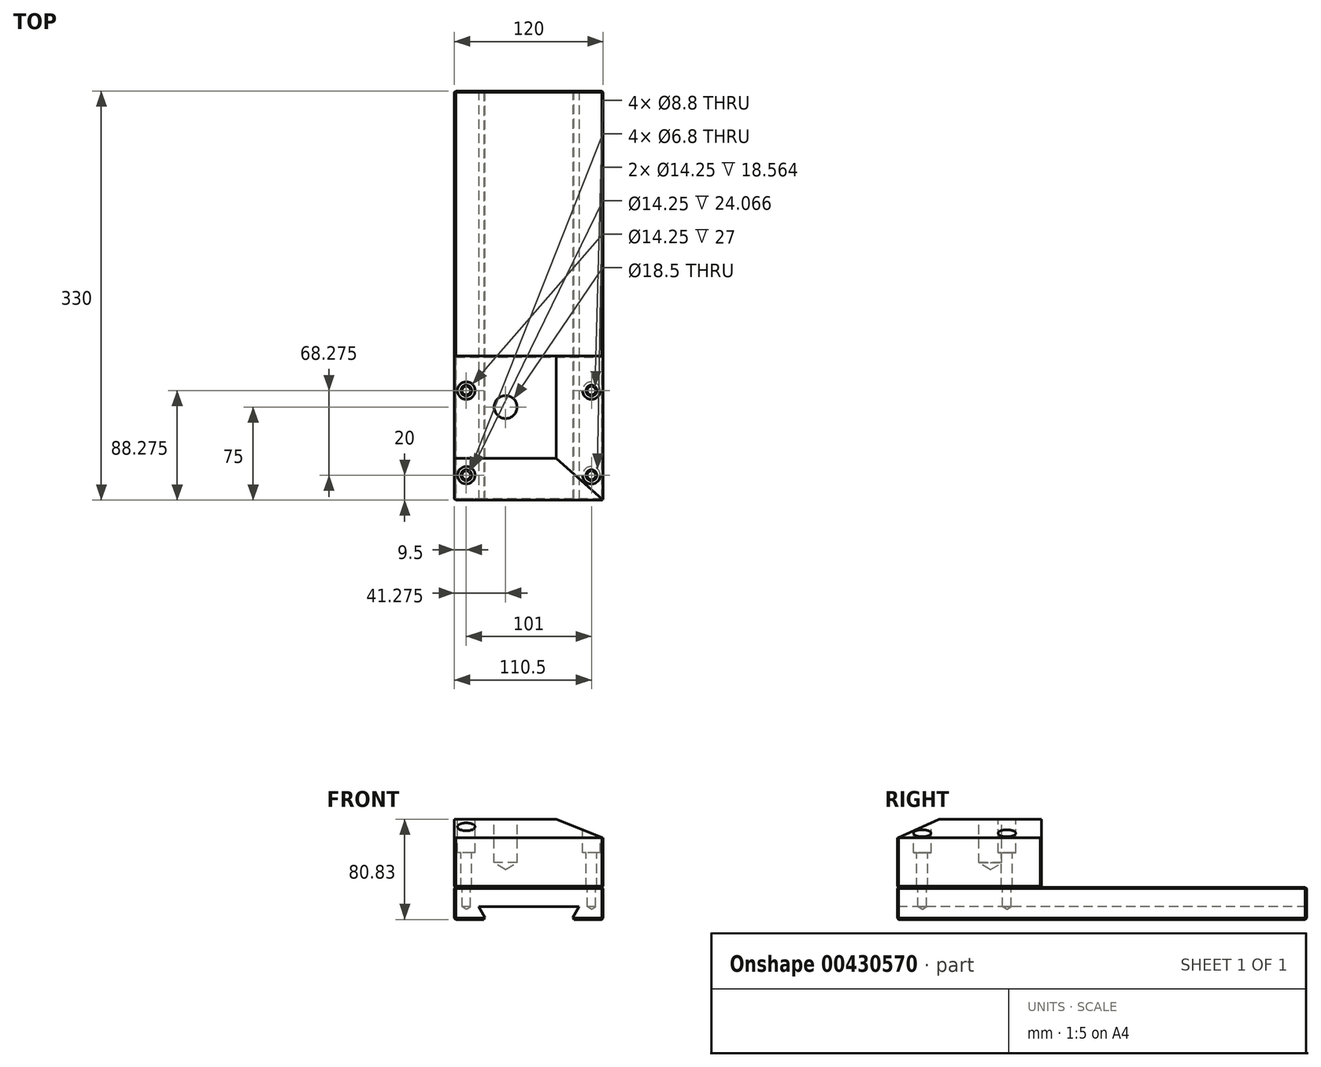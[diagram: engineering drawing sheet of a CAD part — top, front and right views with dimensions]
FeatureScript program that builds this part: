
annotation { "Feature Type Name" : "Feature", "Feature Type Description" : "" }
export const myFeature = defineFeature(function(context is Context, id is Id, definition is map)
    precondition{}
    {
        {
            var Q0;
            Q0=qCreatedBy(makeId("Front.planeOp"),FACE);
            var sketch = newSketch(context, id + "F0", { "sketchPlane" : qUnion([Q0])});
            skLineSegment(sketch, "E0.bottom", {"start": v(0, 0) * mm, "end": v(25.49, 0) * mm});
            skLineSegment(sketch, "E0.top", {"start": v(0, 26) * mm, "end": v(120, 26) * mm});
            skLineSegment(sketch, "E0.left", {"start": v(0, 0) * mm, "end": v(0, 26) * mm});
            skLineSegment(sketch, "E0.right", {"start": v(120, 0) * mm, "end": v(120, 26) * mm});
            skLineSegment(sketch, "E1", {"start": v(19.56, 10.27) * mm, "end": v(25.49, 0) * mm});
            skLineSegment(sketch, "E2", {"start": v(19.56, 10.27) * mm, "end": v(60, 10.27) * mm});
            skLineSegment(sketch, "E3", {"start": v(60, 10.27) * mm, "end": v(100.44, 10.27) * mm});
            skLineSegment(sketch, "E4", {"start": v(100.44, 10.27) * mm, "end": v(94.51, 0) * mm});
            skLineSegment(sketch, "E5", {"start": v(60, -6.52) * mm, "end": v(60, 31.96) * mm, "construction": true});
            skPoint(sketch, "E5.startSnap0", {"position": v(60, 0) * mm});
            skPoint(sketch, "E5.endSnap0", {"position": v(60, 26) * mm});
            skLineSegment(sketch, "E6.trimOffspring", {"start": v(94.51, 0) * mm, "end": v(120, 0) * mm});
            skSolve(sketch);
        }
        {
            var Q0;
            Q0=qSketchRegion(id+"F0",true);
            var Q1;
            Q1=makeQuery(id+"F0.imprint","IMPRINT",FACE,{"disambiguationData":[TD([[makeQuery(id+"F0.imprint","IMPRINT",EDGE,{"derivedFrom":sQuery(id+"F0.wireOp",EDGE,"E0.bottom")}),1.0]])]});
            extrude(context, id + "F1", {"entities" : qUnion([Q0, Q1]), "oppositeDirection" : true, "depth" : 330 * mm});
        }
        {
            var Q0;
            Q0=makeQuery(id+"F1.opExtrude","CAP_FACE",FACE,{"disambiguationData":[OSD([sQuery(id+"F0.wireOp",EDGE,"E0.bottom"),sQuery(id+"F0.wireOp",EDGE,"E0.top"),sQuery(id+"F0.wireOp",EDGE,"E0.left"),sQuery(id+"F0.wireOp",EDGE,"E0.right"),sQuery(id+"F0.wireOp",EDGE,"E1"),sQuery(id+"F0.wireOp",EDGE,"E2"),sQuery(id+"F0.wireOp",EDGE,"E3"),sQuery(id+"F0.wireOp",EDGE,"E4"),sQuery(id+"F0.wireOp",EDGE,"E6.trimOffspring")])],"isStart":true});
            var sketch = newSketch(context, id + "F2", { "sketchPlane" : qUnion([Q0])});
            skLineSegment(sketch, "E7.bottom", {"start": v(0, 26) * mm, "end": v(120, 26) * mm});
            skLineSegment(sketch, "E7.top", {"start": v(0, 80.83) * mm, "end": v(120, 80.83) * mm});
            skLineSegment(sketch, "E7.left", {"start": v(0, 26) * mm, "end": v(0, 80.83) * mm});
            skLineSegment(sketch, "E7.right", {"start": v(120, 26) * mm, "end": v(120, 80.83) * mm});
            skSolve(sketch);
        }
        {
            var Q0;
            Q0=makeQuery(id+"F1.opExtrude","SWEPT_EDGE",EDGE,{"disambiguationData":[OSD([sQuery(id+"F0.wireOp",EDGE,"E0.top"),sQuery(id+"F0.wireOp",EDGE,"E0.left")])]});
            var Q1;
            Q1=makeQuery(id+"F1.opExtrude","SWEPT_EDGE",EDGE,{"disambiguationData":[OSD([sQuery(id+"F0.wireOp",EDGE,"E0.top"),sQuery(id+"F0.wireOp",EDGE,"E0.right")])]});
            var Q2;
            Q2=makeQuery(id+"F1.opExtrude","CAP_EDGE",EDGE,{"disambiguationData":[OSD([sQuery(id+"F0.wireOp",EDGE,"E0.left")])],"isStart":true});
            var Q3;
            Q3=makeQuery(id+"F1.opExtrude","CAP_EDGE",EDGE,{"disambiguationData":[OSD([sQuery(id+"F0.wireOp",EDGE,"E0.right")])],"isStart":true});
            var Q4;
            Q4=makeQuery(id+"F1.opExtrude","CAP_EDGE",EDGE,{"disambiguationData":[OSD([sQuery(id+"F0.wireOp",EDGE,"E6.trimOffspring")])],"isStart":true});
            var Q5;
            Q5=makeQuery(id+"F1.opExtrude","CAP_EDGE",EDGE,{"disambiguationData":[OSD([sQuery(id+"F0.wireOp",EDGE,"E0.bottom")])],"isStart":true});
            var Q6;
            Q6=makeQuery(id+"F1.opExtrude","SWEPT_EDGE",EDGE,{"disambiguationData":[OSD([sQuery(id+"F0.wireOp",EDGE,"E0.bottom"),sQuery(id+"F0.wireOp",EDGE,"E0.left")])]});
            var Q7;
            Q7=makeQuery(id+"F1.opExtrude","CAP_EDGE",EDGE,{"disambiguationData":[OSD([sQuery(id+"F0.wireOp",EDGE,"E0.bottom")])],"isStart":false});
            var Q8;
            Q8=makeQuery(id+"F1.opExtrude","CAP_EDGE",EDGE,{"disambiguationData":[OSD([sQuery(id+"F0.wireOp",EDGE,"E0.left")])],"isStart":false});
            var Q9;
            Q9=makeQuery(id+"F1.opExtrude","CAP_EDGE",EDGE,{"disambiguationData":[OSD([sQuery(id+"F0.wireOp",EDGE,"E0.top")])],"isStart":false});
            var Q10;
            Q10=makeQuery(id+"F1.opExtrude","CAP_EDGE",EDGE,{"disambiguationData":[OSD([sQuery(id+"F0.wireOp",EDGE,"E6.trimOffspring")])],"isStart":false});
            var Q11;
            Q11=makeQuery(id+"F1.opExtrude","CAP_EDGE",EDGE,{"disambiguationData":[OSD([sQuery(id+"F0.wireOp",EDGE,"E0.right")])],"isStart":false});
            var Q12;
            Q12=makeQuery(id+"F1.opExtrude","SWEPT_EDGE",EDGE,{"disambiguationData":[OSD([sQuery(id+"F0.wireOp",EDGE,"E0.right"),sQuery(id+"F0.wireOp",EDGE,"E6.trimOffspring")])]});
            var Q13;
            Q13=makeQuery(id+"F1.opExtrude","SWEPT_EDGE",EDGE,{"disambiguationData":[OSD([sQuery(id+"F0.wireOp",EDGE,"E4"),sQuery(id+"F0.wireOp",EDGE,"E6.trimOffspring")])]});
            var Q14;
            Q14=makeQuery(id+"F1.opExtrude","SWEPT_EDGE",EDGE,{"disambiguationData":[OSD([sQuery(id+"F0.wireOp",EDGE,"E0.bottom"),sQuery(id+"F0.wireOp",EDGE,"E1")])]});
            var Q15;
            Q15=makeQuery(id+"F1.opExtrude","CAP_EDGE",EDGE,{"disambiguationData":[OSD([sQuery(id+"F0.wireOp",EDGE,"E0.top")])],"isStart":true});
            chamfer(context, id + "F3", {"entities" : qUnion([Q0, Q1, Q2, Q3, Q4, Q5, Q6, Q7, Q8, Q9, Q10, Q11, Q12, Q13, Q14, Q15]), "width" : 1 * mm, "tangentPropagation" : true});
        }
        {
            var Q0;
            Q0=qSketchRegion(id+"F2",true);
            extrude(context, id + "F4", {"entities" : qUnion([Q0]), "oppositeDirection" : true, "depth" : 116.28 * mm});
        }
        {
            var Q0;
            Q0=makeQuery(id+"F4.opExtrude","SWEPT_FACE",FACE,{"disambiguationData":[OSD([sQuery(id+"F2.wireOp",EDGE,"E7.top")])]});
            var sketch = newSketch(context, id + "F5", { "sketchPlane" : qUnion([Q0])});
            skLineSegment(sketch, "E8.bottom", {"start": v(9.5, 88.27) * mm, "end": v(110.5, 88.28) * mm, "construction": true});
            skLineSegment(sketch, "E8.top", {"start": v(9.5, 20) * mm, "end": v(110.5, 20) * mm, "construction": true});
            skLineSegment(sketch, "E8.left", {"start": v(9.5, 88.27) * mm, "end": v(9.5, 20) * mm, "construction": true});
            skLineSegment(sketch, "E8.right", {"start": v(110.5, 88.28) * mm, "end": v(110.5, 20) * mm, "construction": true});
            skPoint(sketch, "E9", {"position": v(9.5, 88.27) * mm});
            skPoint(sketch, "E10", {"position": v(110.5, 88.28) * mm});
            skPoint(sketch, "E11", {"position": v(110.5, 20) * mm});
            skPoint(sketch, "E12", {"position": v(9.5, 20) * mm});
            skPoint(sketch, "E13", {"position": v(41.27, 75) * mm});
            skPoint(sketch, "E13.positionSnap0", {"position": v(60, 88.28) * mm});
            skPoint(sketch, "E13.positionSnap1", {"position": v(120, 58.14) * mm});
            skSolve(sketch);
        }
        {
            var Q0;
            Q0=sQuery(id+"F5.wireOp",VERTEX,"E8.bottom.start");
            var Q1;
            Q1=sQuery(id+"F5.wireOp",VERTEX,"E12");
            var Q2;
            Q2=makeQuery(id+"F4.opExtrude","SWEPT_BODY",BODY,{"disambiguationData":[OSD([sQuery(id+"F2.wireOp",EDGE,"E7.bottom"),sQuery(id+"F2.wireOp",EDGE,"E7.top"),sQuery(id+"F2.wireOp",EDGE,"E7.left"),sQuery(id+"F2.wireOp",EDGE,"E7.right")])]});
            hole(context, id + "F6", {"style" : HoleStyle.C_BORE, "endStyle" : HoleEndStyle.THROUGH, "holeDiameter" : 8.8 * mm, "cBoreDiameter" : 14.25 * mm, "cBoreDepth" : 27 * mm, "isTappedThrough" : true, "tappedDepth" : 12 * mm, "tapClearance" : 3, "startFromSketch" : true, "locations" : qUnion([Q0, Q1]), "scope" : qUnion([Q2])});
        }
        {
            var Q0;
            Q0=sQuery(id+"F5.wireOp",VERTEX,"E13");
            var Q1;
            Q1=makeQuery(id+"F4.opExtrude","SWEPT_BODY",BODY,{"disambiguationData":[OSD([sQuery(id+"F2.wireOp",EDGE,"E7.bottom"),sQuery(id+"F2.wireOp",EDGE,"E7.top"),sQuery(id+"F2.wireOp",EDGE,"E7.left"),sQuery(id+"F2.wireOp",EDGE,"E7.right")])]});
            hole(context, id + "F7", {"style" : HoleStyle.SIMPLE, "endStyle" : HoleEndStyle.BLIND, "standardTappedOrClearance" : lookupTablePath({ "standard" : "ISO", "engagement" : "75%", "pitch" : "1.5 mm", "size" : "M20", "type" : "Tapped" }), "standardBlindInLast" : lookupTablePath({ "standard" : "ISO", "engagement" : "75%", "pitch" : "1.5 mm", "size" : "M20", "type" : "Tapped" }), "holeDiameter" : 18.5 * mm, "showTappedDepth" : true, "holeDepth" : 35 * mm, "isTappedThrough" : true, "tappedDepth" : 30.5 * mm, "tapClearance" : 3, "startFromSketch" : true, "locations" : qUnion([Q0]), "scope" : qUnion([Q1]), "majorDiameter" : 20 * mm});
        }
        {
            var Q0;
            Q0=makeQuery(id+"F4.opExtrude","SWEPT_EDGE",EDGE,{"disambiguationData":[OSD([sQuery(id+"F0.wireOp",EDGE,"E0.right"),sQuery(id+"F2.wireOp",EDGE,"E7.bottom"),sQuery(id+"F2.wireOp",EDGE,"E7.right")])]});
            var Q1;
            Q1=makeQuery(id+"F4.opExtrude","CAP_EDGE",EDGE,{"disambiguationData":[OSD([sQuery(id+"F2.wireOp",EDGE,"E7.left")])],"isStart":false});
            var Q2;
            Q2=makeQuery(id+"F4.opExtrude","CAP_EDGE",EDGE,{"disambiguationData":[OSD([sQuery(id+"F2.wireOp",EDGE,"E7.left")])],"isStart":true});
            var Q3;
            Q3=makeQuery(id+"F4.opExtrude","CAP_EDGE",EDGE,{"disambiguationData":[OSD([sQuery(id+"F2.wireOp",EDGE,"E7.right")])],"isStart":true});
            var Q4;
            Q4=makeQuery(id+"F4.opExtrude","SWEPT_EDGE",EDGE,{"disambiguationData":[OSD([sQuery(id+"F0.wireOp",EDGE,"E0.left"),sQuery(id+"F2.wireOp",EDGE,"E7.bottom"),sQuery(id+"F2.wireOp",EDGE,"E7.left")])]});
            var Q5;
            Q5=makeQuery(id+"F4.opExtrude","CAP_EDGE",EDGE,{"disambiguationData":[OSD([sQuery(id+"F2.wireOp",EDGE,"E7.right")])],"isStart":false});
            var Q6;
            Q6=makeQuery(id+"F4.opExtrude","CAP_EDGE",EDGE,{"disambiguationData":[OSD([sQuery(id+"F2.wireOp",EDGE,"E7.bottom")])],"isStart":false});
            var Q7;
            Q7=makeQuery(id+"F4.opExtrude","CAP_EDGE",EDGE,{"disambiguationData":[OSD([sQuery(id+"F2.wireOp",EDGE,"E7.bottom")])],"isStart":true});
            chamfer(context, id + "F8", {"entities" : qUnion([Q0, Q1, Q2, Q3, Q4, Q5, Q6, Q7]), "width" : 1 * mm, "tangentPropagation" : true});
        }
        {
            var Q0;
            Q0=makeQuery(id+"F4.opExtrude","CAP_EDGE",EDGE,{"disambiguationData":[OSD([sQuery(id+"F2.wireOp",EDGE,"E7.top")])],"isStart":true});
            chamfer(context, id + "F9", {"entities" : qUnion([Q0]), "chamferType" : ChamferType.TWO_OFFSETS, "width1" : 33.73 * mm, "oppositeDirection" : false, "width2" : 15 * mm, "tangentPropagation" : true});
        }
        {
            var Q0;
            Q0=makeQuery(id+"F4.opExtrude","SWEPT_EDGE",EDGE,{"disambiguationData":[OSD([sQuery(id+"F2.wireOp",EDGE,"E7.top"),sQuery(id+"F2.wireOp",EDGE,"E7.right")])]});
            chamfer(context, id + "F10", {"entities" : qUnion([Q0]), "chamferType" : ChamferType.TWO_OFFSETS, "width1" : 15 * mm, "oppositeDirection" : false, "width2" : 38 * mm, "tangentPropagation" : true});
        }
        {
            var Q0;
            Q0=makeQuery(id+"F1.opExtrude","SWEPT_FACE",FACE,{"disambiguationData":[OSD([sQuery(id+"F0.wireOp",EDGE,"E0.top")])]});
            var sketch = newSketch(context, id + "F11", { "sketchPlane" : qUnion([Q0])});
            skPoint(sketch, "E14", {"position": v(9.5, 88.28) * mm});
            skPoint(sketch, "E15", {"position": v(9.5, 20) * mm});
            skLineSegment(sketch, "E16", {"start": v(9.5, 20) * mm, "end": v(128.47, 20) * mm, "construction": true});
            skLineSegment(sketch, "E17", {"start": v(110.5, 14.95) * mm, "end": v(110.5, 110.22) * mm, "construction": true});
            skLineSegment(sketch, "E18", {"start": v(9.5, 88.28) * mm, "end": v(113.6, 88.28) * mm, "construction": true});
            skPoint(sketch, "E19", {"position": v(110.5, 20) * mm});
            skPoint(sketch, "E20", {"position": v(110.5, 88.28) * mm});
            skSolve(sketch);
        }
        {
            var Q0;
            Q0=sQuery(id+"F11.wireOp",VERTEX,"E15");
            var Q1;
            Q1=sQuery(id+"F11.wireOp",VERTEX,"E14");
            var Q2;
            Q2=sQuery(id+"F11.wireOp",VERTEX,"E20");
            var Q3;
            Q3=sQuery(id+"F11.wireOp",VERTEX,"E19");
            var Q4;
            Q4=makeQuery(id+"F1.opExtrude","SWEPT_BODY",BODY,{"disambiguationData":[OSD([sQuery(id+"F0.wireOp",EDGE,"E0.bottom"),sQuery(id+"F0.wireOp",EDGE,"E0.top"),sQuery(id+"F0.wireOp",EDGE,"E0.left"),sQuery(id+"F0.wireOp",EDGE,"E0.right"),sQuery(id+"F0.wireOp",EDGE,"E1"),sQuery(id+"F0.wireOp",EDGE,"E2"),sQuery(id+"F0.wireOp",EDGE,"E3"),sQuery(id+"F0.wireOp",EDGE,"E4"),sQuery(id+"F0.wireOp",EDGE,"E6.trimOffspring")])]});
            hole(context, id + "F12", {"style" : HoleStyle.SIMPLE, "endStyle" : HoleEndStyle.BLIND, "standardTappedOrClearance" : lookupTablePath({ "standard" : "ISO", "engagement" : "75%", "pitch" : "1.25 mm", "size" : "M8", "type" : "Tapped" }), "standardBlindInLast" : lookupTablePath({ "standard" : "ISO", "engagement" : "75%", "pitch" : "1.25 mm", "size" : "M8", "type" : "Tapped" }), "holeDiameter" : 6.8 * mm, "showTappedDepth" : true, "holeDepth" : 15.75 * mm, "isTappedThrough" : true, "tappedDepth" : 12 * mm, "tapClearance" : 3, "startFromSketch" : true, "locations" : qUnion([Q0, Q1, Q2, Q3]), "scope" : qUnion([Q4]), "majorDiameter" : 8 * mm});
        }
        {
            var Q0;
            Q0=sQuery(id+"F5.wireOp",VERTEX,"E10");
            var Q1;
            Q1=sQuery(id+"F5.wireOp",VERTEX,"E11");
            var Q2;
            Q2=makeQuery(id+"F4.opExtrude","SWEPT_BODY",BODY,{"disambiguationData":[OSD([sQuery(id+"F2.wireOp",EDGE,"E7.bottom"),sQuery(id+"F2.wireOp",EDGE,"E7.top"),sQuery(id+"F2.wireOp",EDGE,"E7.left"),sQuery(id+"F2.wireOp",EDGE,"E7.right")])]});
            hole(context, id + "F13", {"style" : HoleStyle.C_BORE, "endStyle" : HoleEndStyle.THROUGH, "holeDiameter" : 8.8 * mm, "cBoreDiameter" : 14.25 * mm, "cBoreDepth" : 27 * mm, "isTappedThrough" : true, "tappedDepth" : 12 * mm, "tapClearance" : 3, "startFromSketch" : true, "locations" : qUnion([Q0, Q1]), "scope" : qUnion([Q2])});
        }
    });
